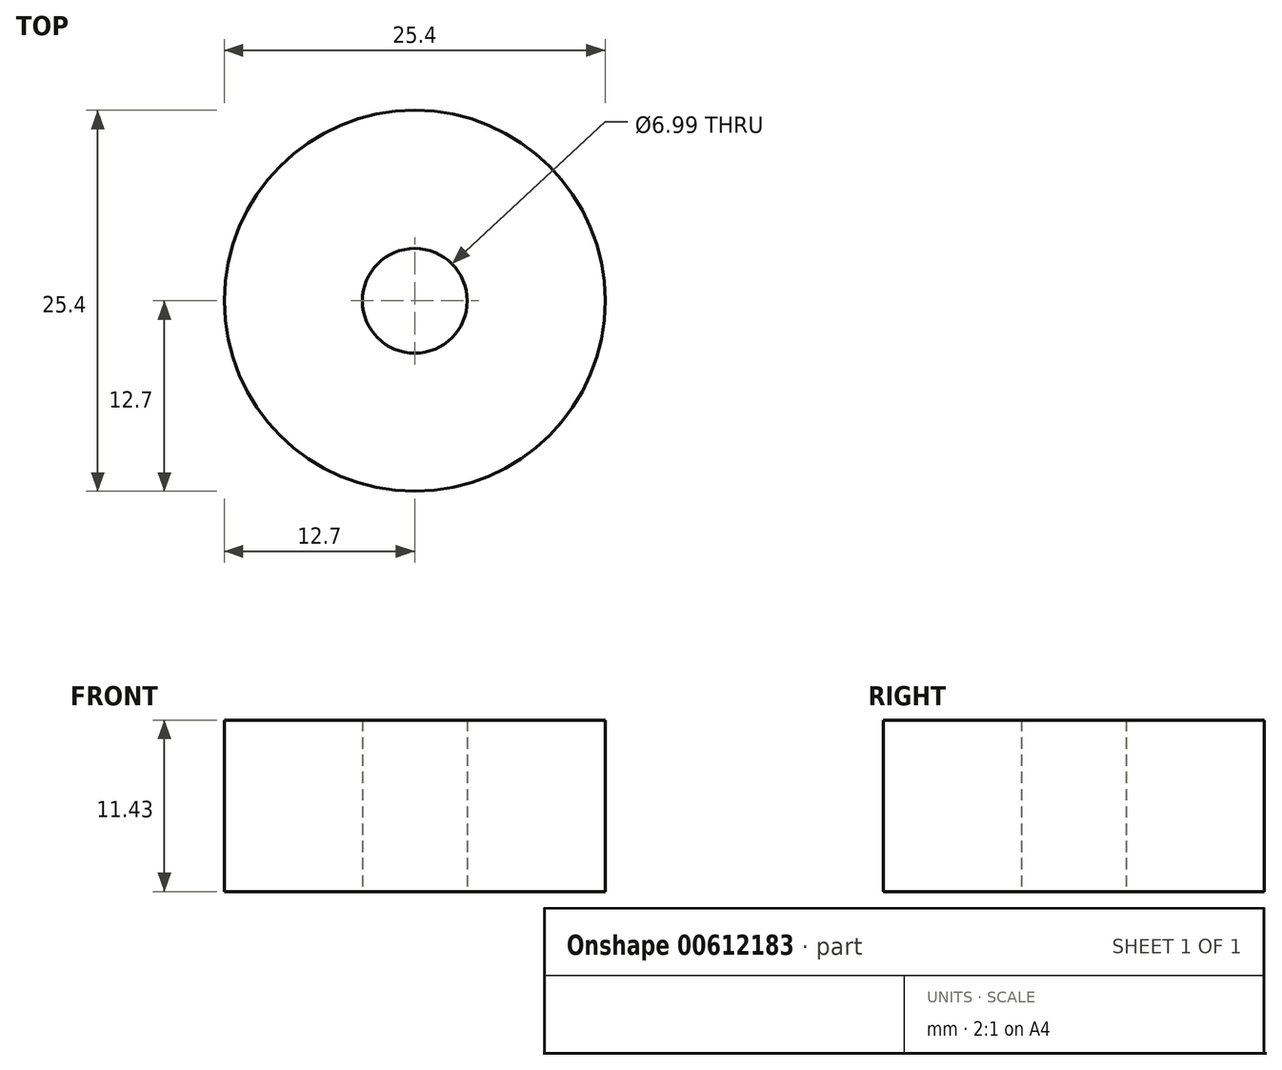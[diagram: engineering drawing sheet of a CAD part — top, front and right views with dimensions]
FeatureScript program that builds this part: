
annotation { "Feature Type Name" : "Feature", "Feature Type Description" : "" }
export const myFeature = defineFeature(function(context is Context, id is Id, definition is map)
    precondition{}
    {
        {
            var Q0;
            Q0=qCreatedBy(makeId("Top.planeOp"),FACE);
            var sketch = newSketch(context, id + "F0", { "sketchPlane" : qUnion([Q0])});
            skCircle(sketch, "E0", {"center": v(0, 0) * mm, "radius": 12.7 * mm});
            skCircle(sketch, "E1", {"center": v(0, 0) * mm, "radius": 3.5 * mm});
            skSolve(sketch);
        }
        {
            var Q0;
            Q0 = qSketchRegion(id + "F0", true);
            extrude(context, id + "F1", {"entities" : qUnion([Q0]), "depth" : 11.43 * mm, "offsetDistance" : 25.4 * mm});
        }
    });
